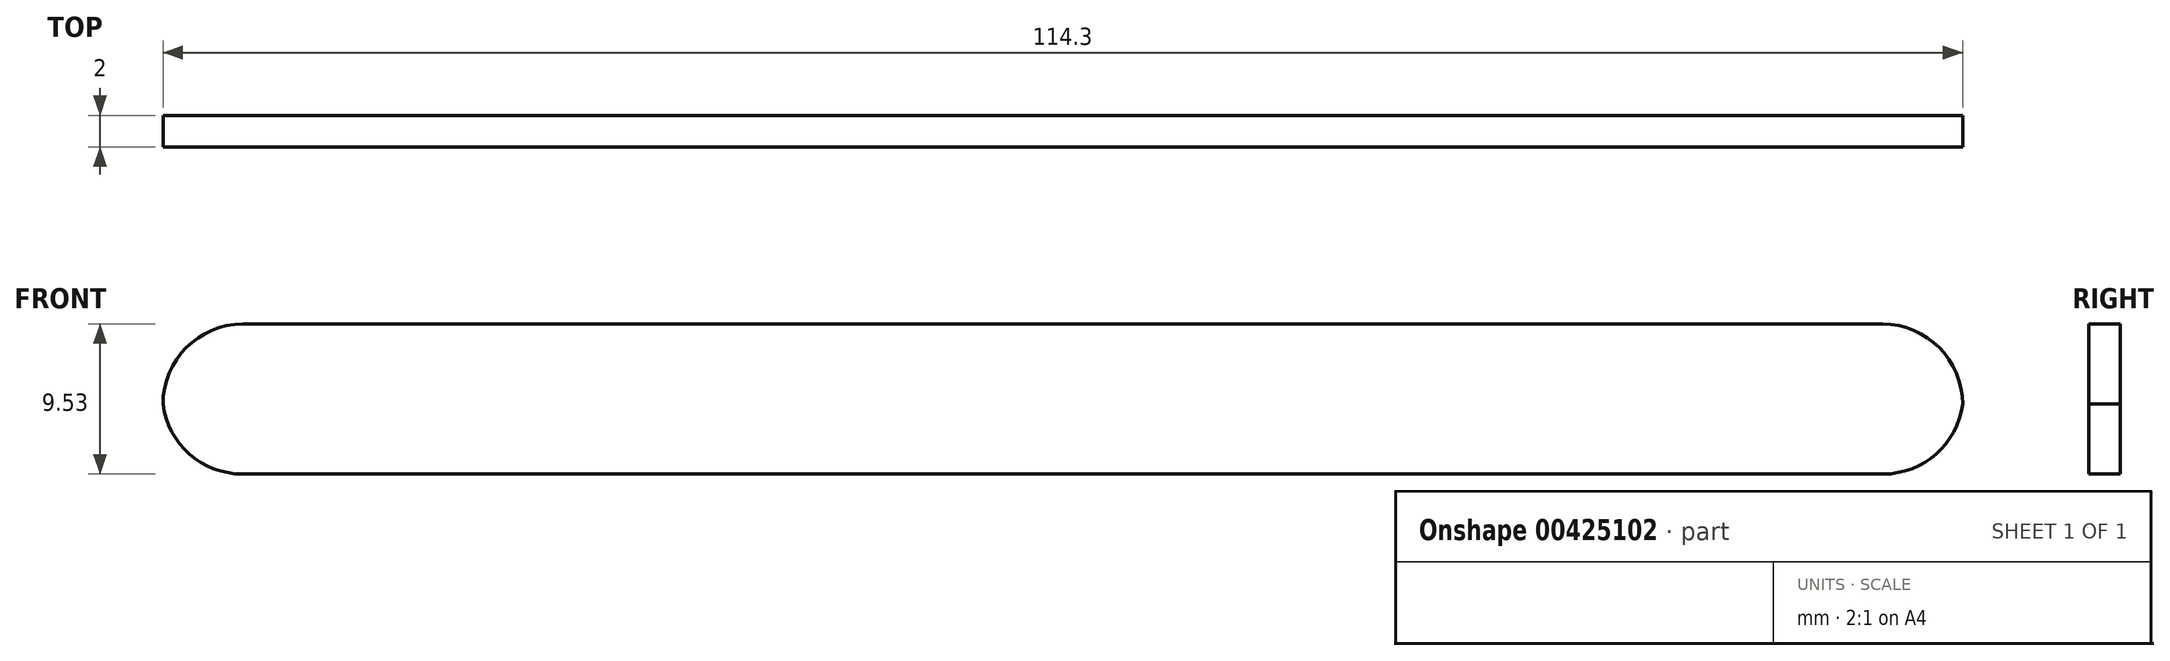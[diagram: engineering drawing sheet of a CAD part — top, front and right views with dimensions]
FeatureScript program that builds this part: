
annotation { "Feature Type Name" : "Feature", "Feature Type Description" : "" }
export const myFeature = defineFeature(function(context is Context, id is Id, definition is map)
    precondition{}
    {
        {
            var Q0;
            Q0=qCreatedBy(makeId("Front.planeOp"),FACE);
            var sketch = newSketch(context, id + "F0", { "sketchPlane" : qUnion([Q0])});
            skLineSegment(sketch, "E0.bottom", {"start": v(-51.76, -9.8) * mm, "end": v(62.54, -9.8) * mm});
            skLineSegment(sketch, "E0.top", {"start": v(-51.76, -19.32) * mm, "end": v(62.54, -19.32) * mm});
            skLineSegment(sketch, "E0.left", {"start": v(-51.76, -9.8) * mm, "end": v(-51.76, -19.32) * mm});
            skLineSegment(sketch, "E0.right", {"start": v(62.54, -9.8) * mm, "end": v(62.54, -19.32) * mm});
            skSolve(sketch);
        }
        {
            var Q0;
            Q0 = qSketchRegion(id + "F0", true);
            extrude(context, id + "F1", {"entities" : qUnion([Q0]), "depth" : 2 * mm});
        }
        {
            var Q0;
            Q0=makeQuery(id+"F1.opExtrude","SWEPT_EDGE",EDGE,{"disambiguationData":[OSD([sQuery(id+"F0.wireOp",EDGE,"E0.bottom"),sQuery(id+"F0.wireOp",EDGE,"E0.left")])]});
            fillet(context, id + "F2", {"entities" : qUnion([Q0]), "radius" : 5.08 * mm, "tangentPropagation" : true, "allowEdgeOverflow" : false});
        }
        {
            var Q0;
            Q0=makeQuery(id+"F1.opExtrude","SWEPT_EDGE",EDGE,{"disambiguationData":[OSD([sQuery(id+"F0.wireOp",EDGE,"E0.top"),sQuery(id+"F0.wireOp",EDGE,"E0.left")])]});
            fillet(context, id + "F3", {"entities" : qUnion([Q0]), "radius" : 5.08 * mm, "tangentPropagation" : true, "allowEdgeOverflow" : false});
        }
        {
            var Q0;
            Q0=makeQuery(id+"F1.opExtrude","SWEPT_EDGE",EDGE,{"disambiguationData":[OSD([sQuery(id+"F0.wireOp",EDGE,"E0.bottom"),sQuery(id+"F0.wireOp",EDGE,"E0.right")])]});
            fillet(context, id + "F4", {"entities" : qUnion([Q0]), "radius" : 5.08 * mm, "tangentPropagation" : true, "allowEdgeOverflow" : false});
        }
        {
            var Q0;
            Q0=makeQuery(id+"F1.opExtrude","SWEPT_EDGE",EDGE,{"disambiguationData":[OSD([sQuery(id+"F0.wireOp",EDGE,"E0.top"),sQuery(id+"F0.wireOp",EDGE,"E0.right")])]});
            fillet(context, id + "F5", {"entities" : qUnion([Q0]), "radius" : 5.08 * mm, "tangentPropagation" : true, "allowEdgeOverflow" : false});
        }
    });
